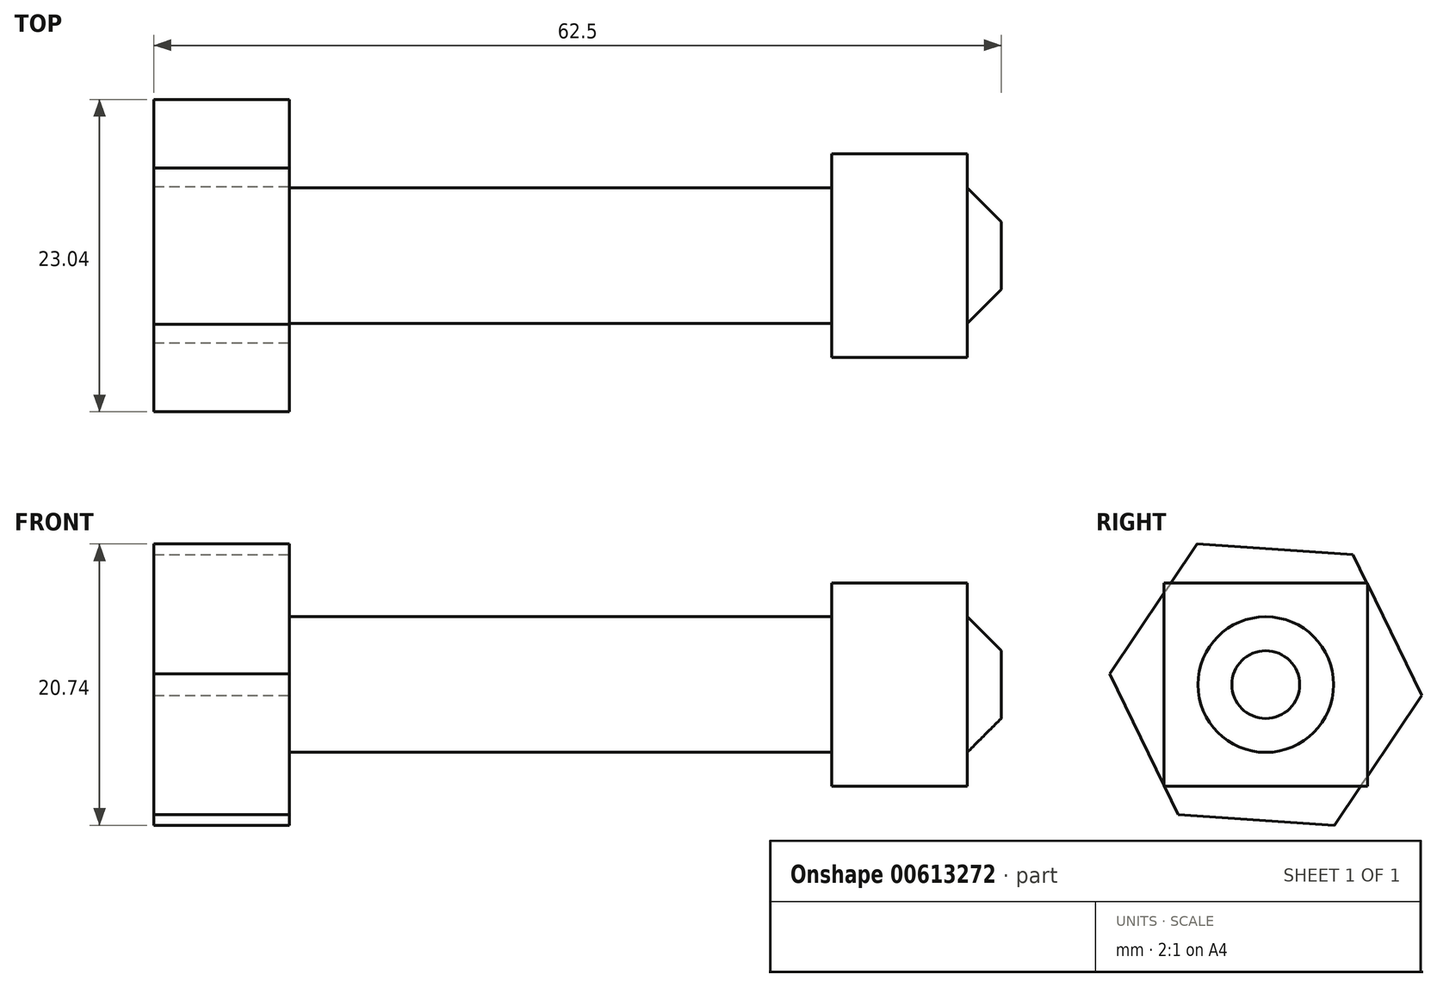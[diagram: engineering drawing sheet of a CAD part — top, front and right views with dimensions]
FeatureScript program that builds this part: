
annotation { "Feature Type Name" : "Feature", "Feature Type Description" : "" }
export const myFeature = defineFeature(function(context is Context, id is Id, definition is map)
    precondition{}
    {
        {
            var Q0;
            Q0=qCreatedBy(makeId("Right.planeOp"),FACE);
            var sketch = newSketch(context, id + "F0", { "sketchPlane" : qUnion([Q0])});
            skCircle(sketch, "E0", {"center": v(0, 0) * mm, "radius": 5 * mm});
            skSolve(sketch);
        }
        {
            var Q0;
            Q0 = qSketchRegion(id + "F0", true);
            extrude(context, id + "F1", {"entities" : qUnion([Q0]), "depth" : 50 * mm, "offsetDistance" : 25 * mm});
        }
        {
            var Q0;
            Q0=makeQuery(id+"F1.opExtrude","CAP_FACE",FACE,{"disambiguationData":[OSD([sQuery(id+"F0.wireOp",EDGE,"E0")])],"isStart":true});
            var sketch = newSketch(context, id + "F2", { "sketchPlane" : qUnion([Q0])});
            skCircle(sketch, "E1.cCircle", {"center": v(0, 0) * mm, "radius": 10 * mm, "construction": true});
            skLineSegment(sketch, "E1.0", {"start": v(5.08, 10.37) * mm, "end": v(11.52, 0.79) * mm});
            skLineSegment(sketch, "E1.1", {"start": v(11.52, 0.79) * mm, "end": v(6.44, -9.58) * mm});
            skLineSegment(sketch, "E1.2", {"start": v(6.44, -9.58) * mm, "end": v(-5.08, -10.37) * mm});
            skLineSegment(sketch, "E1.3", {"start": v(-5.08, -10.37) * mm, "end": v(-11.52, -0.79) * mm});
            skLineSegment(sketch, "E1.4", {"start": v(-11.52, -0.79) * mm, "end": v(-6.44, 9.58) * mm});
            skLineSegment(sketch, "E1.5", {"start": v(-6.44, 9.58) * mm, "end": v(5.08, 10.37) * mm});
            skSolve(sketch);
        }
        {
            var Q0;
            Q0 = qSketchRegion(id + "F2", true);
            extrude(context, id + "F3", {"entities" : qUnion([Q0]), "operationType" : NewBodyOperationType.ADD, "depth" : 10 * mm, "offsetDistance" : 25 * mm});
        }
        {
            var Q0;
            Q0=makeQuery(id+"F1.opExtrude","CAP_FACE",FACE,{"disambiguationData":[OSD([sQuery(id+"F0.wireOp",EDGE,"E0")])],"isStart":false});
            var sketch = newSketch(context, id + "F4", { "sketchPlane" : qUnion([Q0])});
            skLineSegment(sketch, "E2.bottom", {"start": v(7.5, 7.5) * mm, "end": v(-7.5, 7.5) * mm});
            skLineSegment(sketch, "E2.top", {"start": v(7.5, -7.5) * mm, "end": v(-7.5, -7.5) * mm});
            skLineSegment(sketch, "E2.left", {"start": v(7.5, 7.5) * mm, "end": v(7.5, -7.5) * mm});
            skLineSegment(sketch, "E2.right", {"start": v(-7.5, 7.5) * mm, "end": v(-7.5, -7.5) * mm});
            skPoint(sketch, "E2.middle", {"position": v(0, 0) * mm});
            skSolve(sketch);
        }
        {
            var Q0;
            Q0=makeQuery(id+"F4.imprint","IMPRINT",FACE,{"disambiguationData":[TD([[makeQuery(id+"F4.imprint","IMPRINT",EDGE,{"derivedFrom":sQuery(id+"F4.wireOp",EDGE,"E2.bottom")}),1.0]])]});
            extrude(context, id + "F5", {"entities" : qUnion([Q0]), "operationType" : NewBodyOperationType.ADD, "oppositeDirection" : true, "depth" : 10 * mm, "offsetDistance" : 25 * mm});
        }
        {
            var Q0;
            {var subQ0=sQuery(id+"F0.wireOp",EDGE,"E0");Q0=makeQuery(id+"F5.boolean.opBoolean","MERGE",FACE,{"derivedFrom":[makeQuery(id+"F1.opExtrude","CAP_FACE",FACE,{"disambiguationData":[OSD([subQ0])],"isStart":false}),makeQuery(id+"F5.opExtrude","CAP_FACE",FACE,{"disambiguationData":[OSD([subQ0,sQuery(id+"F4.wireOp",EDGE,"E2.bottom"),sQuery(id+"F4.wireOp",EDGE,"E2.top"),sQuery(id+"F4.wireOp",EDGE,"E2.left"),sQuery(id+"F4.wireOp",EDGE,"E2.right")])],"isStart":true})]});}
            var sketch = newSketch(context, id + "F6", { "sketchPlane" : qUnion([Q0])});
            skCircle(sketch, "E3", {"center": v(0, 0) * mm, "radius": 5 * mm});
            skSolve(sketch);
        }
        {
            var Q0;
            Q0 = qSketchRegion(id + "F6", true);
            extrude(context, id + "F7", {"entities" : qUnion([Q0]), "operationType" : NewBodyOperationType.ADD, "depth" : 2.5 * mm, "offsetDistance" : 25 * mm});
        }
        {
            var Q0;
            Q0=makeQuery(id+"F7.opExtrude","CAP_EDGE",EDGE,{"disambiguationData":[OSD([sQuery(id+"F6.wireOp",EDGE,"E3")])],"isStart":false});
            chamfer(context, id + "F8", {"entities" : qUnion([Q0]), "width" : 2.5 * mm, "tangentPropagation" : true});
        }
    });
